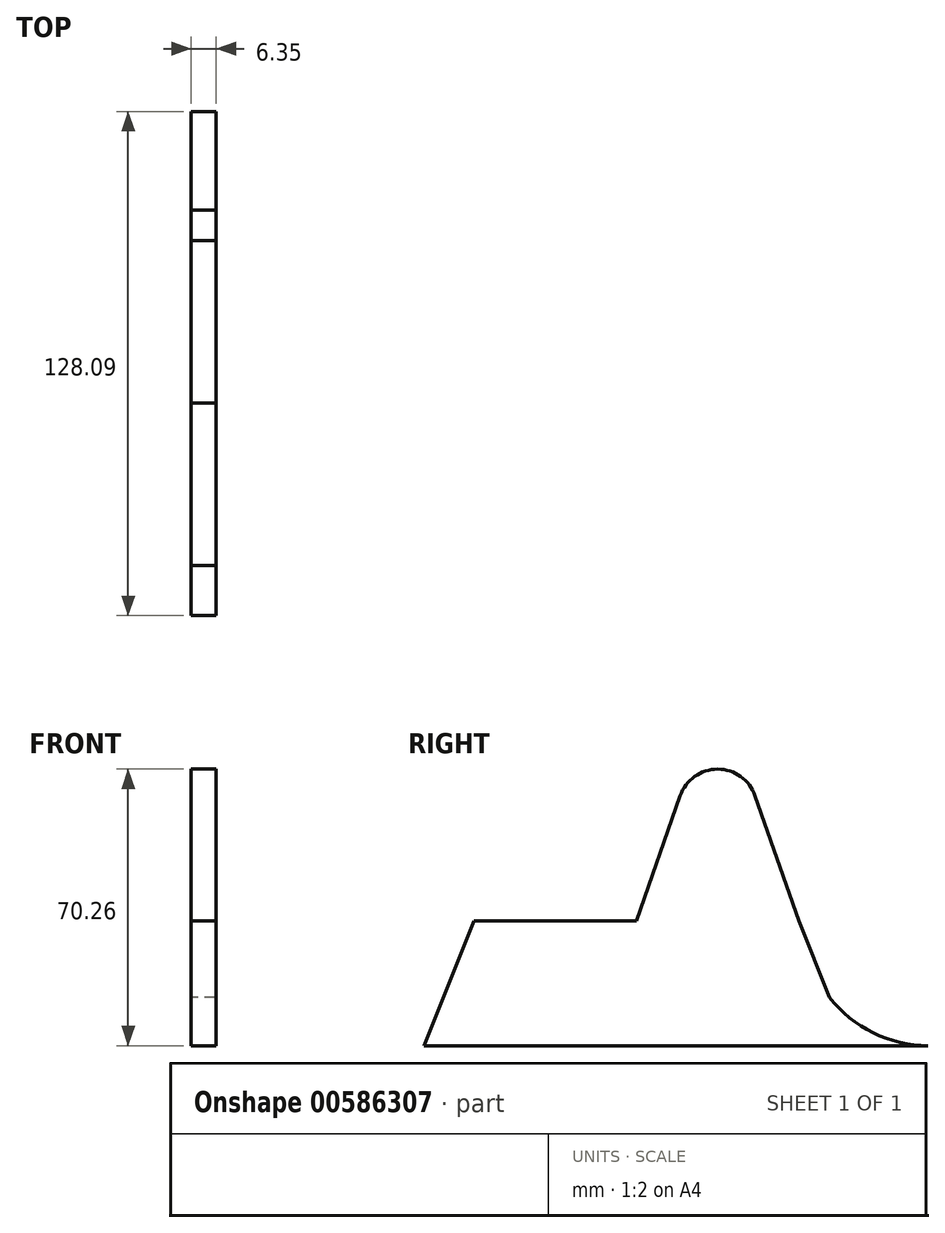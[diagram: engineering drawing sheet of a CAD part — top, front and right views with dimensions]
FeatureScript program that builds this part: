
annotation { "Feature Type Name" : "Feature", "Feature Type Description" : "" }
export const myFeature = defineFeature(function(context is Context, id is Id, definition is map)
    precondition{}
    {
        {
            var Q0;
            Q0=qCreatedBy(makeId("Right.planeOp"),FACE);
            var sketch = newSketch(context, id + "F0", { "sketchPlane" : qUnion([Q0])});
            skLineSegment(sketch, "E0", {"start": v(0, 0) * mm, "end": v(53.98, 0) * mm});
            skLineSegment(sketch, "E1", {"start": v(49.05, 12.31) * mm, "end": v(41.27, 31.75) * mm});
            skLineSegment(sketch, "E2.MirrorCS", {"start": v(-41.28, 31.75) * mm, "end": v(0, 31.75) * mm});
            skLineSegment(sketch, "E3.MirrorCS", {"start": v(-53.98, 0) * mm, "end": v(-41.27, 31.75) * mm});
            skLineSegment(sketch, "E4.MirrorCS", {"start": v(0, 0) * mm, "end": v(-53.98, 0) * mm});
            skPoint(sketch, "E5.endSnap0", {"position": v(20.64, 31.75) * mm});
            skLineSegment(sketch, "E6", {"start": v(30.16, 63.5) * mm, "end": v(41.28, 31.75) * mm});
            skLineSegment(sketch, "E7", {"start": v(11.11, 63.5) * mm, "end": v(0, 31.75) * mm});
            skArc(sketch, "E8", {"start": v(30.16, 63.5) * mm, "mid": v(20.64, 70.26) * mm, "end": v(11.11, 63.5) * mm});
            skLineSegment(sketch, "E9", {"start": v(53.98, 0) * mm, "end": v(74.1, 0) * mm});
            skArc(sketch, "E10", {"start": v(49.05, 12.31) * mm, "mid": v(60.15, 3.24) * mm, "end": v(74.1, 0) * mm});
            skPoint(sketch, "E11.end.orphan", {"position": v(20.64, 70.26) * mm});
            skPoint(sketch, "E11.start.orphan", {"position": v(20.64, 63.5) * mm});
            skSolve(sketch);
        }
        {
            var Q0;
            Q0=makeQuery(id+"F0.imprint","IMPRINT",FACE,{"disambiguationData":[TD([[makeQuery(id+"F0.imprint","IMPRINT",EDGE,{"derivedFrom":sQuery(id+"F0.wireOp",EDGE,"E0")}),1.0]])]});
            extrude(context, id + "F1", {"entities" : qUnion([Q0]), "depth" : 6.35 * mm, "offsetDistance" : 25.4 * mm});
        }
    });
